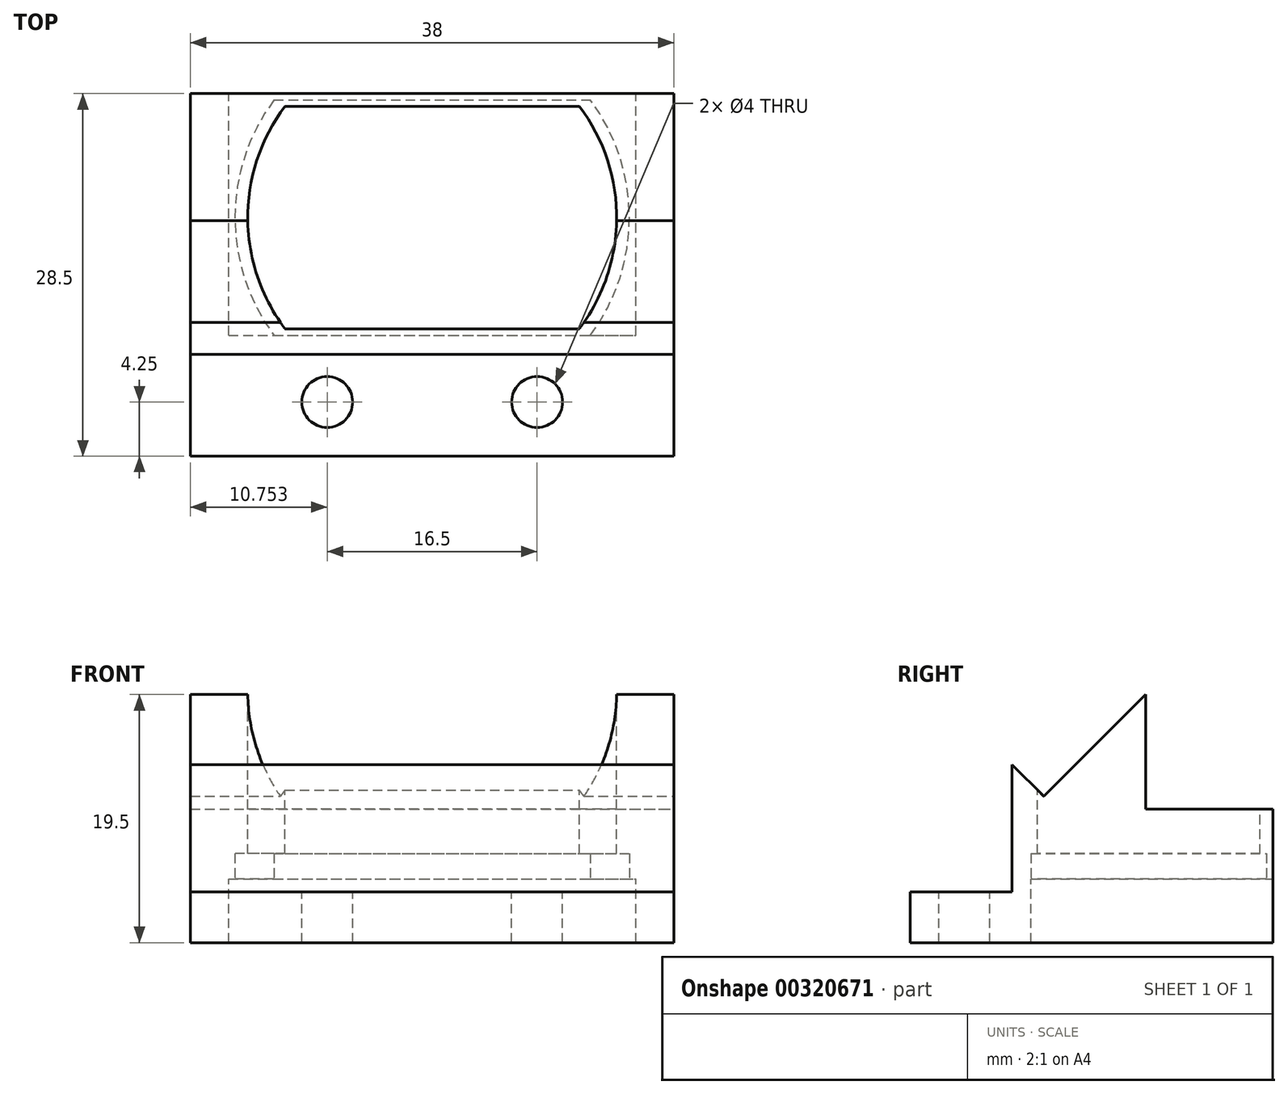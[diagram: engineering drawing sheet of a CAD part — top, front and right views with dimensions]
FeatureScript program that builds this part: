
annotation { "Feature Type Name" : "Feature", "Feature Type Description" : "" }
export const myFeature = defineFeature(function(context is Context, id is Id, definition is map)
    precondition{}
    {
        {
            var Q0;
            Q0=qCreatedBy(makeId("Top.planeOp"),FACE);
            var sketch = newSketch(context, id + "F0", { "sketchPlane" : qUnion([Q0])});
            skLineSegment(sketch, "E0.bottom", {"start": v(-15.89, 0) * mm, "end": v(22.11, 0) * mm});
            skLineSegment(sketch, "E0.top", {"start": v(-15.89, 28.5) * mm, "end": v(22.11, 28.5) * mm});
            skLineSegment(sketch, "E0.left", {"start": v(-15.89, 0) * mm, "end": v(-15.89, 28.5) * mm});
            skLineSegment(sketch, "E0.right", {"start": v(22.11, 0) * mm, "end": v(22.11, 28.5) * mm});
            skSolve(sketch);
        }
        {
            var Q0;
            Q0 = qSketchRegion(id + "F0", true);
            extrude(context, id + "F1", {"entities" : qUnion([Q0]), "flatOperationType" : FlatOperationType.REMOVE, "offsetDistance" : 25 * mm, "depth" : 19.5 * mm, "domain" : OperationDomain.MODEL});
        }
        {
            var Q0;
            Q0=makeQuery(id+"F1.opExtrude","SWEPT_FACE",FACE,{"disambiguationData":[OSD([sQuery(id+"F0.wireOp",EDGE,"E0.right")])]});
            var sketch = newSketch(context, id + "F2", { "sketchPlane" : qUnion([Q0])});
            skLineSegment(sketch, "E1.bottom", {"start": v(0, 19.5) * mm, "end": v(8, 19.5) * mm});
            skLineSegment(sketch, "E1.top", {"start": v(0, 4) * mm, "end": v(8, 4) * mm});
            skLineSegment(sketch, "E1.left", {"start": v(0, 19.5) * mm, "end": v(0, 4) * mm});
            skLineSegment(sketch, "E1.right", {"start": v(8, 19.5) * mm, "end": v(8, 4) * mm});
            skSolve(sketch);
        }
        {
            var Q0;
            {var subQ4=sQuery(id+"F2.wireOp",EDGE,"E1.top");Q0=makeQuery(id+"F2.imprint","IMPRINT",FACE,{"disambiguationData":[TD([[makeQuery(id+"F2.imprint","IMPRINT",EDGE,{"derivedFrom":subQ4}),-1.0]])]});}
            var sketch = newSketch(context, id + "F3", { "sketchPlane" : qUnion([Q0])});
            skLineSegment(sketch, "E2.bottom", {"start": v(28.5, 19.5) * mm, "end": v(18.5, 19.5) * mm});
            skLineSegment(sketch, "E2.top", {"start": v(28.5, 10.5) * mm, "end": v(18.5, 10.5) * mm});
            skLineSegment(sketch, "E2.left", {"start": v(28.5, 19.5) * mm, "end": v(28.5, 10.5) * mm});
            skLineSegment(sketch, "E2.right", {"start": v(18.5, 19.5) * mm, "end": v(18.5, 10.5) * mm});
            skSolve(sketch);
        }
        {
            var Q0;
            Q0=makeQuery(id+"F2.imprint","IMPRINT",FACE,{"disambiguationData":[TD([[makeQuery(id+"F2.imprint","IMPRINT",EDGE,{"derivedFrom":sQuery(id+"F2.wireOp",EDGE,"E1.bottom")}),-1.0]])]});
            extrude(context, id + "F4", {"entities" : qUnion([Q0]), "operationType" : NewBodyOperationType.REMOVE, "oppositeDirection" : true, "depth" : 38 * mm});
        }
        {
            var Q0;
            Q0=makeQuery(id+"F1.opExtrude","CAP_FACE",FACE,{"disambiguationData":[OSD([sQuery(id+"F0.wireOp",EDGE,"E0.bottom"),sQuery(id+"F0.wireOp",EDGE,"E0.top"),sQuery(id+"F0.wireOp",EDGE,"E0.left"),sQuery(id+"F0.wireOp",EDGE,"E0.right")])],"isStart":false});
            var sketch = newSketch(context, id + "F5", { "sketchPlane" : qUnion([Q0])});
            skLineSegment(sketch, "E3.bottom", {"start": v(-8.45, 10) * mm, "end": v(14.68, 10) * mm});
            skLineSegment(sketch, "E3.top", {"start": v(-8.45, 27.5) * mm, "end": v(14.68, 27.5) * mm});
            skArc(sketch, "E4", {"start": v(14.68, 10) * mm, "mid": v(17.61, 18.75) * mm, "end": v(14.68, 27.5) * mm});
            skArc(sketch, "E5.trimOffspring", {"start": v(-8.45, 27.5) * mm, "mid": v(-11.39, 18.75) * mm, "end": v(-8.45, 10) * mm});
            skSolve(sketch);
        }
        {
            var Q0;
            Q0 = qSketchRegion(id + "F5", true);
            extrude(context, id + "F6", {"entities" : qUnion([Q0]), "operationType" : NewBodyOperationType.REMOVE, "oppositeDirection" : true, "depth" : 19.5 * mm});
        }
        {
            var Q0;
            Q0=makeQuery(id+"F3.imprint","IMPRINT",FACE,{"disambiguationData":[TD([[makeQuery(id+"F3.imprint","IMPRINT",EDGE,{"derivedFrom":sQuery(id+"F3.wireOp",EDGE,"E2.bottom")}),-1.0]])]});
            extrude(context, id + "F7", {"entities" : qUnion([Q0]), "operationType" : NewBodyOperationType.REMOVE, "oppositeDirection" : true, "depth" : 38 * mm});
        }
        {
            var Q0;
            Q0=makeQuery(id+"F1.opExtrude","SWEPT_FACE",FACE,{"disambiguationData":[OSD([sQuery(id+"F0.wireOp",EDGE,"E0.right")])]});
            var sketch = newSketch(context, id + "F8", { "sketchPlane" : qUnion([Q0])});
            skLineSegment(sketch, "E6.bottom", {"start": v(8, 19.5) * mm, "end": v(18.5, 19.5) * mm});
            skLineSegment(sketch, "E6.left", {"start": v(8, 19.5) * mm, "end": v(8, 14) * mm});
            skLineSegment(sketch, "E7", {"start": v(18.5, 19.5) * mm, "end": v(10.5, 11.5) * mm});
            skLineSegment(sketch, "E8", {"start": v(8, 14) * mm, "end": v(10.5, 11.5) * mm});
            skSolve(sketch);
        }
        {
            var Q0;
            Q0 = qSketchRegion(id + "F8", true);
            extrude(context, id + "F9", {"entities" : qUnion([Q0]), "operationType" : NewBodyOperationType.REMOVE, "oppositeDirection" : true, "depth" : 38 * mm});
        }
        {
            var Q0;
            Q0=makeQuery(id+"F1.opExtrude","CAP_FACE",FACE,{"disambiguationData":[OSD([sQuery(id+"F0.wireOp",EDGE,"E0.bottom"),sQuery(id+"F0.wireOp",EDGE,"E0.top"),sQuery(id+"F0.wireOp",EDGE,"E0.left"),sQuery(id+"F0.wireOp",EDGE,"E0.right")])],"isStart":true});
            var sketch = newSketch(context, id + "F10", { "sketchPlane" : qUnion([Q0])});
            skLineSegment(sketch, "E9.bottom", {"start": v(-9.32, -9.5) * mm, "end": v(15.55, -9.5) * mm});
            skLineSegment(sketch, "E9.top", {"start": v(-9.32, -28) * mm, "end": v(15.55, -28) * mm});
            skArc(sketch, "E10", {"start": v(-9.32, -9.5) * mm, "mid": v(-12.39, -18.75) * mm, "end": v(-9.32, -28) * mm});
            skArc(sketch, "E11.trimOffspring", {"start": v(15.55, -28) * mm, "mid": v(18.61, -18.75) * mm, "end": v(15.55, -9.5) * mm});
            skSolve(sketch);
        }
        {
            var Q0;
            Q0 = qSketchRegion(id + "F10", true);
            extrude(context, id + "F11", {"entities" : qUnion([Q0]), "operationType" : NewBodyOperationType.REMOVE, "oppositeDirection" : true, "depth" : 7 * mm});
        }
        {
            var Q0;
            Q0=makeQuery(id+"F1.opExtrude","SWEPT_FACE",FACE,{"disambiguationData":[OSD([sQuery(id+"F0.wireOp",EDGE,"E0.top")])]});
            var sketch = newSketch(context, id + "F12", { "sketchPlane" : qUnion([Q0])});
            skLineSegment(sketch, "E12.bottom", {"start": v(12.89, 0) * mm, "end": v(-19.11, 0) * mm});
            skLineSegment(sketch, "E12.top", {"start": v(12.89, 5) * mm, "end": v(-19.11, 5) * mm});
            skLineSegment(sketch, "E12.left", {"start": v(12.89, 0) * mm, "end": v(12.89, 5) * mm});
            skLineSegment(sketch, "E12.right", {"start": v(-19.11, 0) * mm, "end": v(-19.11, 5) * mm});
            skSolve(sketch);
        }
        {
            var Q0;
            Q0 = qSketchRegion(id + "F12", true);
            extrude(context, id + "F13", {"entities" : qUnion([Q0]), "operationType" : NewBodyOperationType.REMOVE, "oppositeDirection" : true, "depth" : 19 * mm});
        }
        {
            var Q0;
            Q0=makeQuery(id+"F4.boolean.opBoolean","COPY",FACE,{"derivedFrom":makeQuery(id+"F4.opExtrude","SWEPT_FACE",FACE,{"disambiguationData":[OSD([sQuery(id+"F2.wireOp",EDGE,"E1.top")])]})});
            var sketch = newSketch(context, id + "F14", { "sketchPlane" : qUnion([Q0])});
            skCircle(sketch, "E13", {"center": v(-5.14, 4.25) * mm, "radius": 2 * mm});
            skCircle(sketch, "E14", {"center": v(11.36, 4.25) * mm, "radius": 2 * mm});
            skSolve(sketch);
        }
        {
            var Q0;
            Q0=makeQuery(id+"F14.imprint","IMPRINT",FACE,{"disambiguationData":[TD([[makeQuery(id+"F14.imprint","IMPRINT",EDGE,{"derivedFrom":sQuery(id+"F14.wireOp",EDGE,"E13")}),1.0]])]});
            var Q1;
            Q1=makeQuery(id+"F14.imprint","IMPRINT",FACE,{"disambiguationData":[TD([[makeQuery(id+"F14.imprint","IMPRINT",EDGE,{"derivedFrom":sQuery(id+"F14.wireOp",EDGE,"E14")}),1.0]])]});
            extrude(context, id + "F15", {"entities" : qUnion([Q0, Q1]), "operationType" : NewBodyOperationType.REMOVE, "oppositeDirection" : true, "depth" : 4 * mm});
        }
    });
